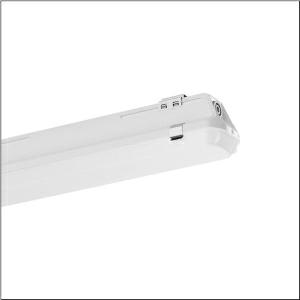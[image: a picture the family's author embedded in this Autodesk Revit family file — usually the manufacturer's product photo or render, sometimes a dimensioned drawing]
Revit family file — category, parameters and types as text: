
# Revit family: monsun_r__21_51fb20dp460b_2c2a
name_source: partatom
category: Lighting Fixtures
units: mm (PartAtom-declared; Revit-internal decimal feet)

## family parameters
Cut with Voids When Loaded = No
Host = Face
Light Source = No
Part Type = Normal
Room Calculation Point = No
Round Connector Dimension = Use Diameter
Shared = No

## types (1)
- --- (1 x LED, 5460 lm, 39.4 W, 4000K)
    Apparent Load = 39 VA
    CIE Flux Codes = 45 75 93 94 100
    Color Rendering = 80
    Color Temperature = 4000K
    Default Elevation = 1800 mm
    Description = Monsun® 21, damp-proof luminaire, chain hanger, primary optical cover: enclosure, of PC, light emission: direct distribution, primary light characteristic: symmetric, installation type: suspended mounting, surface-mounted, horizontal mounting, vertical mounting, LED, rated luminous flux: 5.460lm, luminous efficacy: 139lm/W, light colour: 840, colour temperature: 4000K, control gear: ECG DALI, with terminal, 5-pole, max. 2.5mm², mains connection: 220..240V, AC, 50/60Hz, rated input power: 39W, housing, of glass-fibre reinforced polyester, uncoated, bright grey, incl. chain hanger, length: 1.590mm, width: 90mm, height: 88mm, clip for enclosure, of stainless steel (V2A), ceiling mounting element, of stainless steel (V2A), chain hanger, of stainless steel (V2A), protection rating (complete): IP66, insulation class (complete): insulation class I (protective earthing), certification: CE, ENEC, VDE, UKCA, protection symbol: D, impact resistance: IK08, permissible operating ambient temperature: -25..+35°C, standard: EN 50419, EN 60598-2-1, corresponds to IFS (International Featured Standards) requirements for safety and quality in the food industry, for indoor or canopied outdoor use, no direct snow, no direct sun, no direct rain, contact your sales advisor before using the luminaires in applications with unclear chemical exposure, large temperature fluctuations or condensation-forming humidity, LABS conformity tested according to VDMA 24364:2018-05, packaging unit: 1 piece
    Height = 89 mm
    Lamp = 1 x LED
    Lamp Light Flux = 5460 lm
    Lamp Power = 39.4 W
    Lamp count = 1
    Length = 1590 mm
    Luminous efficacy = 139 lm/W
    Manufacturer = Siteco
    ModVariant = No
    Model = 51FB20DP460B
    Mounting Place = Ceiling
    Mounting Type = Surface mounted
    Number of Poles = 1
    OnlyDefault = Yes
    Power Factor = 1
    Product Name = Monsun® 21
    Product group = damp-proof luminaire
    ProductGroupID = 300
    Protection Class = Protection class I
    Protection Degree = IP 66
    RLX_Detail_Level = 1
    RLX_Emergency_Light_Flux = 0 lm
    RLX_Emergency_Type = 0
    RLX_Emergency_Type_DB = No
    RlxData = <blob elided: 92289 chars, md5=8eb5a8ea>
    Socket = socket
    Standby Power = 0 W
    System Light Flux = 5460 lm
    System Power = 39 W
    Type Comments = factory setting: luminous flux: 100 % | dim-lin: 254 | 261 mA
    Type Image = l_1319656.jpg
    URL = http://relux.com
    VarID = @adj_171087
    Voltage = 0 V
    Weight = 0.00 kg
    Width = 90 mm

## geometry (parser evidence)
native form markers: Blend x4, Sweep x14
no freeform markers — native parametric forms only
